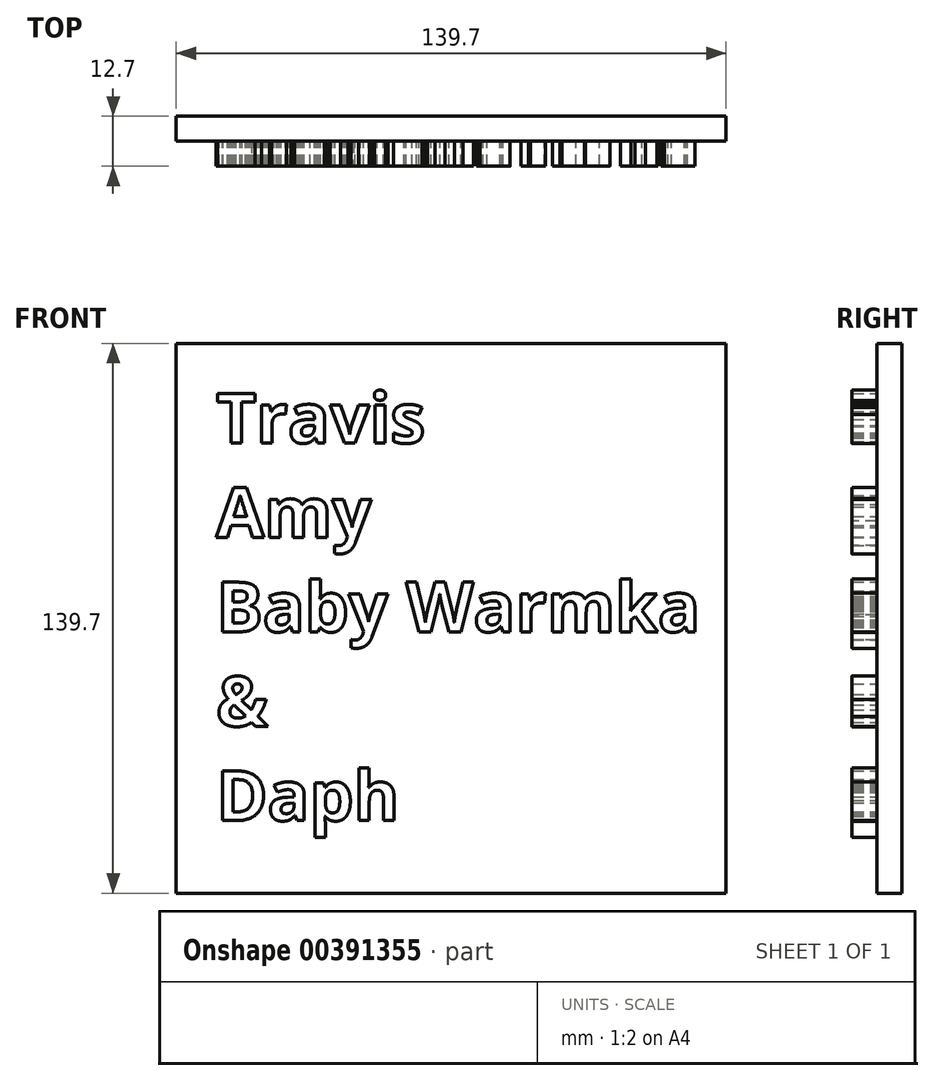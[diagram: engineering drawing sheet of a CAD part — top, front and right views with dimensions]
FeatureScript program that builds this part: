
annotation { "Feature Type Name" : "Feature", "Feature Type Description" : "" }
export const myFeature = defineFeature(function(context is Context, id is Id, definition is map)
    precondition{}
    {
        {
            var Q0;
            Q0=qCreatedBy(makeId("Front.planeOp"),FACE);
            var sketch = newSketch(context, id + "F0", { "sketchPlane" : qUnion([Q0])});
            skText(sketch, "E0", { "text": "Travis\nAmy\nBaby Warmka\n& \nDaph", "fontName": "OpenSans-Bold.ttf"});
            const initialGuessF0  = {"E0": [-0.02105, 0.0021, 1, 0, 0.0127]};
            skSetInitialGuess(sketch, initialGuessF0);
            skSolve(sketch);
        }
        {
            var Q0;
            Q0 = qSketchRegion(id + "F0", true);
            extrude(context, id + "F1", {"entities" : qUnion([Q0]), "depth" : 12.7 * mm});
        }
        {
            var Q0;
            Q0=qCreatedBy(makeId("Front.planeOp"),FACE);
            var sketch = newSketch(context, id + "F2", { "sketchPlane" : qUnion([Q0])});
            skLineSegment(sketch, "E1.bottom", {"start": v(-31.2, 27.39) * mm, "end": v(108.5, 27.39) * mm});
            skLineSegment(sketch, "E1.top", {"start": v(-31.2, -112.31) * mm, "end": v(108.5, -112.31) * mm});
            skLineSegment(sketch, "E1.left", {"start": v(-31.2, 27.39) * mm, "end": v(-31.2, -112.31) * mm});
            skLineSegment(sketch, "E1.right", {"start": v(108.5, 27.39) * mm, "end": v(108.5, -112.31) * mm});
            skSolve(sketch);
        }
        {
            var Q0;
            Q0=makeQuery(id+"F2.imprint","IMPRINT",FACE,{"disambiguationData":[TD([[makeQuery(id+"F2.imprint","IMPRINT",EDGE,{"derivedFrom":sQuery(id+"F2.wireOp",EDGE,"E1.bottom")}),-1.0]])]});
            extrude(context, id + "F3", {"entities" : qUnion([Q0]), "operationType" : NewBodyOperationType.ADD, "depth" : 6.35 * mm});
        }
    });
